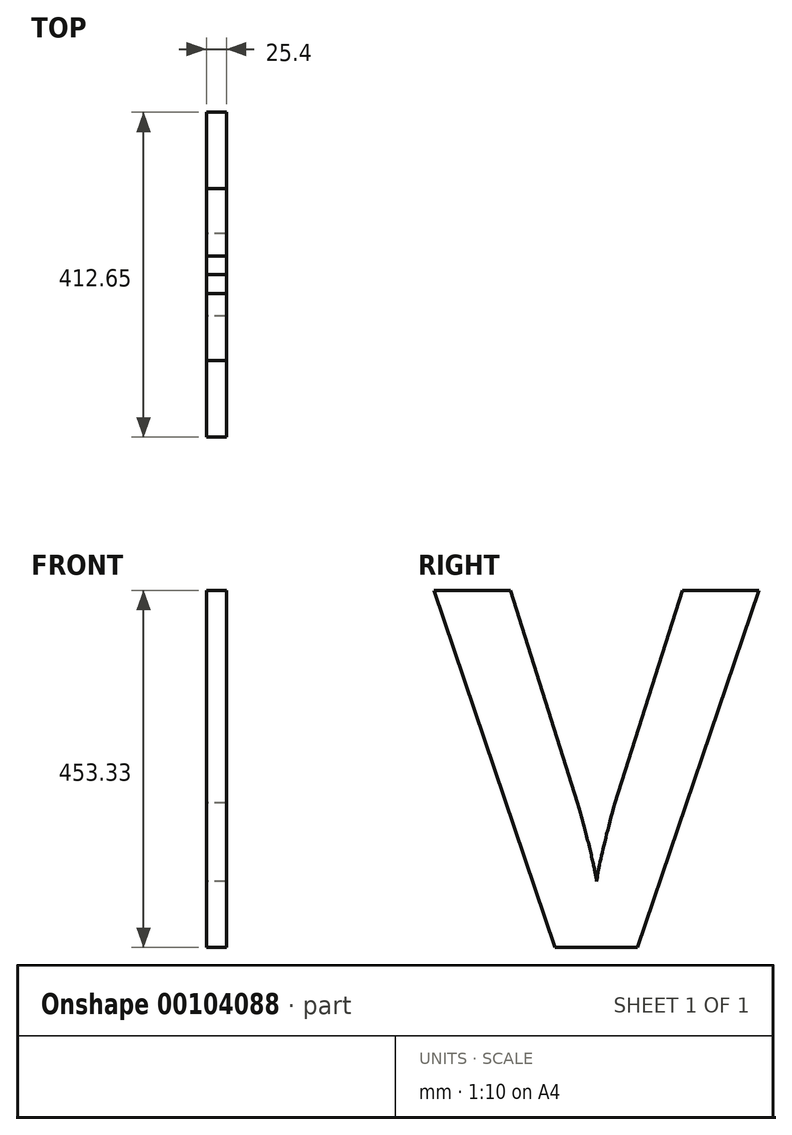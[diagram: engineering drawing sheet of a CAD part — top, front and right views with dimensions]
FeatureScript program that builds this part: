
annotation { "Feature Type Name" : "Feature", "Feature Type Description" : "" }
export const myFeature = defineFeature(function(context is Context, id is Id, definition is map)
    precondition{}
    {
        {
            var Q0;
            Q0=qCreatedBy(makeId("Right.planeOp"),FACE);
            var sketch = newSketch(context, id + "F0", { "sketchPlane" : qUnion([Q0])});
            skText(sketch, "E0", { "text": "V\n", "fontName": "OpenSans-Bold.ttf"});
            const initialGuessF0  = {"E0": [-0.41265, 0, 1, 0, 0.4572]};
            skSetInitialGuess(sketch, initialGuessF0);
            skSolve(sketch);
        }
        {
            var Q0;
            Q0 = qSketchRegion(id + "F0", true);
            extrude(context, id + "F1", {"entities" : qUnion([Q0]), "endBound" : BoundingType.SYMMETRIC, "depth" : 25.4 * mm});
        }
    });
